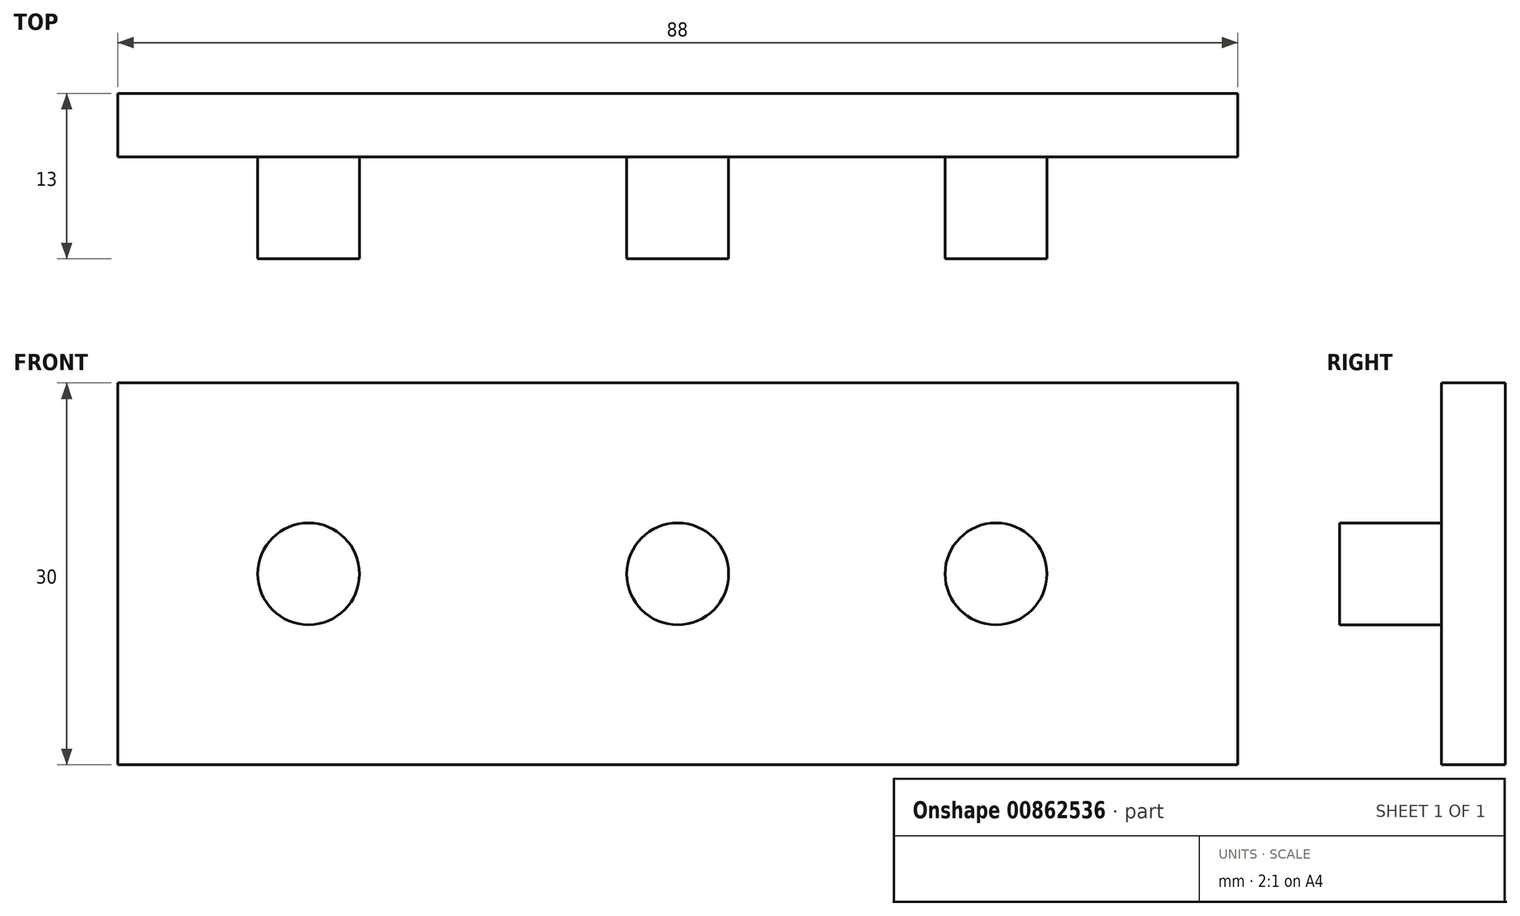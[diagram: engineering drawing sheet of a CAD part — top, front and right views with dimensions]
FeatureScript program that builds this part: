
annotation { "Feature Type Name" : "Feature", "Feature Type Description" : "" }
export const myFeature = defineFeature(function(context is Context, id is Id, definition is map)
    precondition{}
    {
        {
            var Q0;
            Q0=qCreatedBy(makeId("Front.planeOp"),FACE);
            var sketch = newSketch(context, id + "F0", { "sketchPlane" : qUnion([Q0])});
            skLineSegment(sketch, "E0.bottom", {"start": v(44, 15) * mm, "end": v(-44, 15) * mm});
            skLineSegment(sketch, "E0.top", {"start": v(44, -15) * mm, "end": v(-44, -15) * mm});
            skLineSegment(sketch, "E0.left", {"start": v(44, 15) * mm, "end": v(44, -15) * mm});
            skLineSegment(sketch, "E0.right", {"start": v(-44, 15) * mm, "end": v(-44, -15) * mm});
            skPoint(sketch, "E0.middle", {"position": v(0, 0) * mm});
            skSolve(sketch);
        }
        {
            var Q0;
            Q0 = qSketchRegion(id + "F0", true);
            extrude(context, id + "F1", {"entities" : qUnion([Q0]), "depth" : 5 * mm, "offsetDistance" : 25 * mm});
        }
        {
            var Q0;
            Q0=makeQuery(id+"F1.opExtrude","CAP_FACE",FACE,{"disambiguationData":[OSD([sQuery(id+"F0.wireOp",EDGE,"E0.bottom"),sQuery(id+"F0.wireOp",EDGE,"E0.top"),sQuery(id+"F0.wireOp",EDGE,"E0.left"),sQuery(id+"F0.wireOp",EDGE,"E0.right")])],"isStart":false});
            var sketch = newSketch(context, id + "F2", { "sketchPlane" : qUnion([Q0])});
            skCircle(sketch, "E1", {"center": v(-29, 0) * mm, "radius": 4 * mm});
            skSolve(sketch);
        }
        {
            var Q0;
            Q0 = qSketchRegion(id + "F2", true);
            extrude(context, id + "F3", {"entities" : qUnion([Q0]), "operationType" : NewBodyOperationType.ADD, "depth" : 8 * mm, "offsetDistance" : 25 * mm});
        }
        {
            var Q0;
            Q0=makeQuery(id+"F1.opExtrude","CAP_FACE",FACE,{"disambiguationData":[OSD([sQuery(id+"F0.wireOp",EDGE,"E0.bottom"),sQuery(id+"F0.wireOp",EDGE,"E0.top"),sQuery(id+"F0.wireOp",EDGE,"E0.left"),sQuery(id+"F0.wireOp",EDGE,"E0.right")])],"isStart":false});
            var sketch = newSketch(context, id + "F4", { "sketchPlane" : qUnion([Q0])});
            skCircle(sketch, "E2", {"center": v(0, 0) * mm, "radius": 4 * mm});
            skCircle(sketch, "E3", {"center": v(25, 0) * mm, "radius": 4 * mm});
            skSolve(sketch);
        }
        {
            var Q0;
            Q0=makeQuery(id+"F4.imprint","IMPRINT",FACE,{"disambiguationData":[TD([[makeQuery(id+"F4.imprint","IMPRINT",EDGE,{"derivedFrom":sQuery(id+"F4.wireOp",EDGE,"E2")}),1.0]])]});
            var Q1;
            Q1=makeQuery(id+"F4.imprint","IMPRINT",FACE,{"disambiguationData":[TD([[makeQuery(id+"F4.imprint","IMPRINT",EDGE,{"derivedFrom":sQuery(id+"F4.wireOp",EDGE,"E3")}),1.0]])]});
            extrude(context, id + "F5", {"entities" : qUnion([Q0, Q1]), "operationType" : NewBodyOperationType.ADD, "depth" : 8 * mm, "offsetDistance" : 25 * mm});
        }
    });
